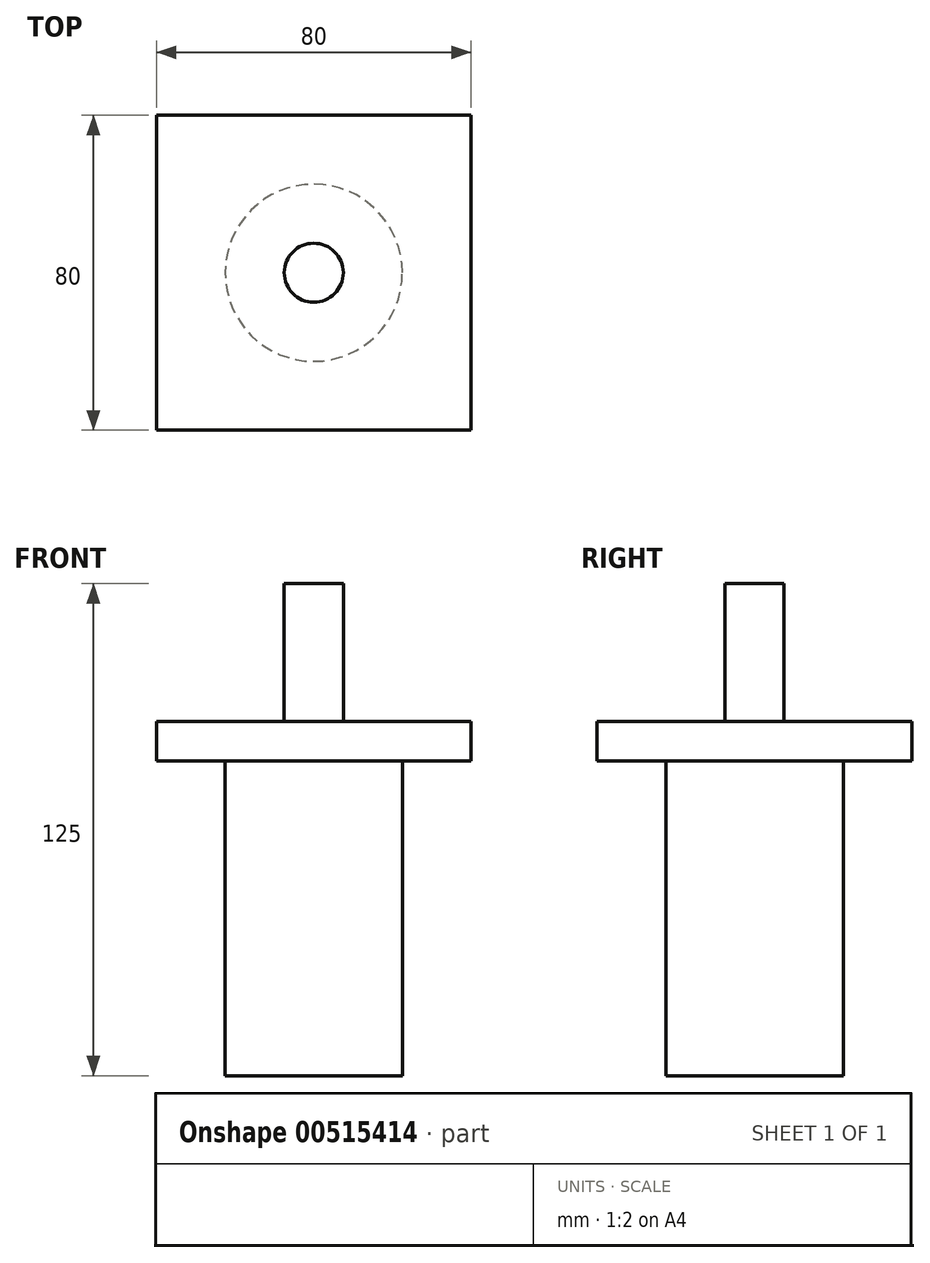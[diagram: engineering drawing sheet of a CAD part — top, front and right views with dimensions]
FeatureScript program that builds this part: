
annotation { "Feature Type Name" : "Feature", "Feature Type Description" : "" }
export const myFeature = defineFeature(function(context is Context, id is Id, definition is map)
    precondition{}
    {
        {
            var Q0;
            Q0=qCreatedBy(makeId("Top.planeOp"),FACE);
            var sketch = newSketch(context, id + "F0", { "sketchPlane" : qUnion([Q0])});
            skLineSegment(sketch, "E0.bottom", {"start": v(40, 40) * mm, "end": v(-40, 40) * mm});
            skLineSegment(sketch, "E0.top", {"start": v(40, -40) * mm, "end": v(-40, -40) * mm});
            skLineSegment(sketch, "E0.left", {"start": v(40, 40) * mm, "end": v(40, -40) * mm});
            skLineSegment(sketch, "E0.right", {"start": v(-40, 40) * mm, "end": v(-40, -40) * mm});
            skPoint(sketch, "E0.middle", {"position": v(0, 0) * mm});
            skSolve(sketch);
        }
        {
            var Q0;
            Q0=makeQuery(id+"F0.imprint","IMPRINT",FACE,{"disambiguationData":[TD([[makeQuery(id+"F0.imprint","IMPRINT",EDGE,{"derivedFrom":sQuery(id+"F0.wireOp",EDGE,"E0.bottom")}),1.0]])]});
            extrude(context, id + "F1", {"entities" : qUnion([Q0]), "oppositeDirection" : true, "depth" : 10 * mm, "offsetDistance" : 25 * mm});
        }
        {
            var Q0;
            Q0=makeQuery(id+"F1.opExtrude","CAP_FACE",FACE,{"disambiguationData":[OSD([sQuery(id+"F0.wireOp",EDGE,"E0.bottom"),sQuery(id+"F0.wireOp",EDGE,"E0.top"),sQuery(id+"F0.wireOp",EDGE,"E0.left"),sQuery(id+"F0.wireOp",EDGE,"E0.right")])],"isStart":false});
            var sketch = newSketch(context, id + "F2", { "sketchPlane" : qUnion([Q0])});
            skCircle(sketch, "E1", {"center": v(0, 0) * mm, "radius": 22.5 * mm});
            skSolve(sketch);
        }
        {
            var Q0;
            Q0=makeQuery(id+"F2.imprint","IMPRINT",FACE,{"disambiguationData":[TD([[makeQuery(id+"F2.imprint","IMPRINT",EDGE,{"derivedFrom":sQuery(id+"F2.wireOp",EDGE,"E1")}),1.0]])]});
            extrude(context, id + "F3", {"entities" : qUnion([Q0]), "operationType" : NewBodyOperationType.ADD, "depth" : 80 * mm, "offsetDistance" : 25 * mm});
        }
        {
            var Q0;
            Q0=makeQuery(id+"F1.opExtrude","CAP_FACE",FACE,{"disambiguationData":[OSD([sQuery(id+"F0.wireOp",EDGE,"E0.bottom"),sQuery(id+"F0.wireOp",EDGE,"E0.top"),sQuery(id+"F0.wireOp",EDGE,"E0.left"),sQuery(id+"F0.wireOp",EDGE,"E0.right")])],"isStart":true});
            var sketch = newSketch(context, id + "F4", { "sketchPlane" : qUnion([Q0])});
            skCircle(sketch, "E2", {"center": v(0, 0) * mm, "radius": 7.5 * mm});
            skSolve(sketch);
        }
        {
            var Q0;
            Q0=makeQuery(id+"F4.imprint","IMPRINT",FACE,{"disambiguationData":[TD([[makeQuery(id+"F4.imprint","IMPRINT",EDGE,{"derivedFrom":sQuery(id+"F4.wireOp",EDGE,"E2")}),1.0]])]});
            extrude(context, id + "F5", {"entities" : qUnion([Q0]), "operationType" : NewBodyOperationType.ADD, "depth" : 35 * mm, "offsetDistance" : 25 * mm});
        }
    });
